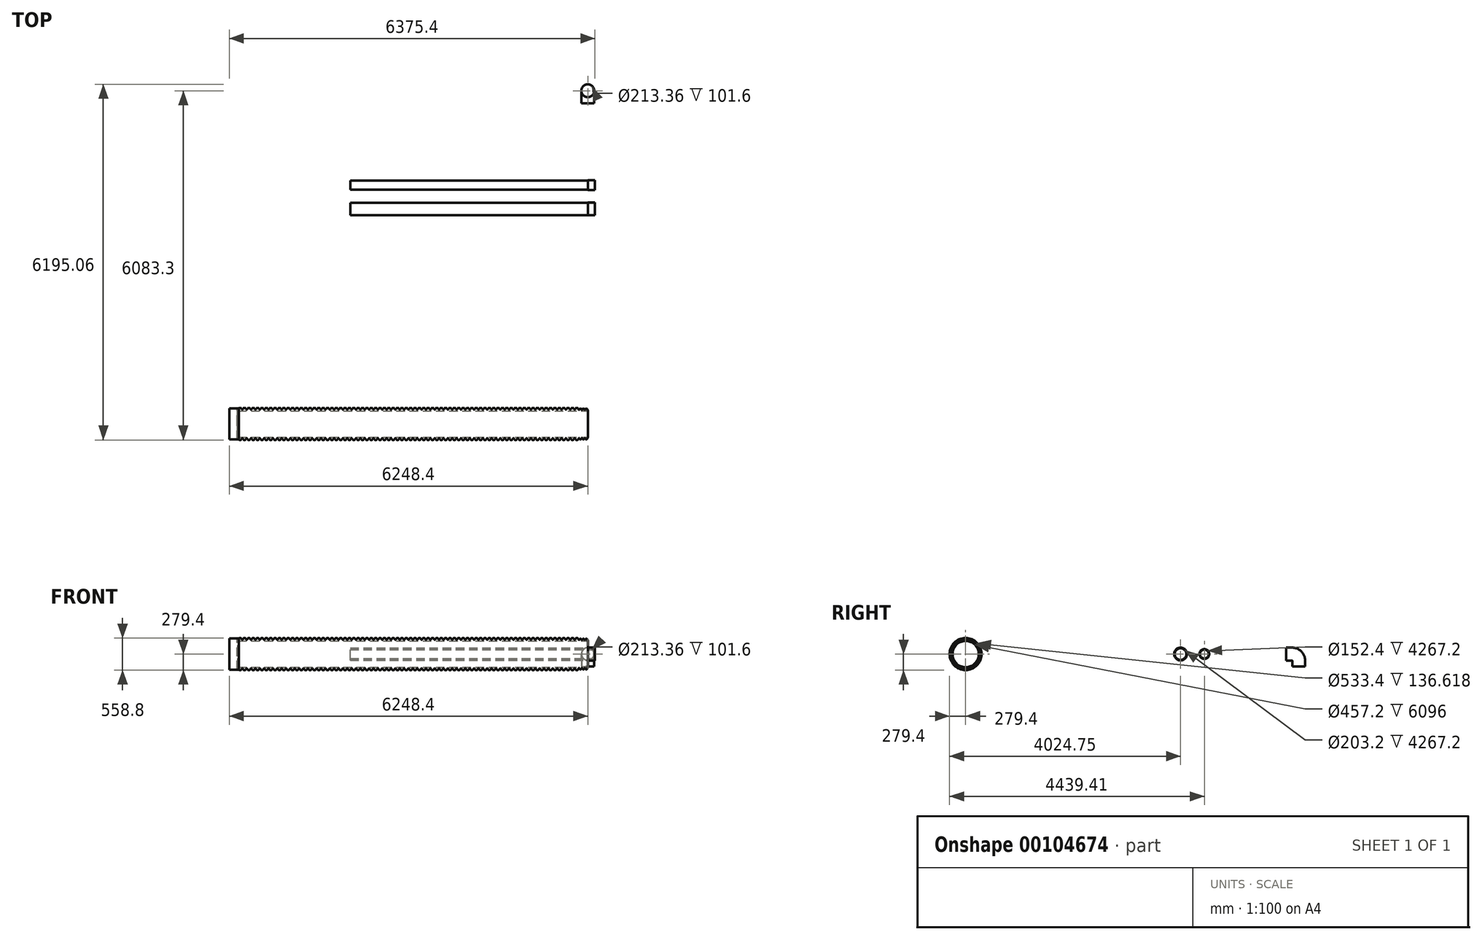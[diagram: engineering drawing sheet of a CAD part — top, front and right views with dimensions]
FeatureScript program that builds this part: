
annotation { "Feature Type Name" : "Feature", "Feature Type Description" : "" }
export const myFeature = defineFeature(function(context is Context, id is Id, definition is map)
    precondition{}
    {
        {
            var Q0;
            Q0=qCreatedBy(makeId("Right.planeOp"),FACE);
            var sketch = newSketch(context, id + "F0", { "sketchPlane" : qUnion([Q0])});
            skLineSegment(sketch, "E0", {"start": v(0, 0) * mm, "end": v(3048, 0) * mm, "construction": true});
            skCircle(sketch, "E1", {"center": v(0, 0) * mm, "radius": 228.6 * mm});
            skCircle(sketch, "E2", {"center": v(0, 0) * mm, "radius": 279.4 * mm});
            skCircle(sketch, "E3", {"center": v(697.35, 0) * mm, "radius": 106.68 * mm});
            skCircle(sketch, "E4", {"center": v(697.35, 0) * mm, "radius": 101.6 * mm});
            skCircle(sketch, "E5", {"center": v(1112.01, 0) * mm, "radius": 76.2 * mm});
            skCircle(sketch, "E6", {"center": v(1112.01, 0) * mm, "radius": 81.28 * mm});
            skCircle(sketch, "E7", {"center": v(697.35, 0) * mm, "radius": 111.76 * mm});
            skCircle(sketch, "E8", {"center": v(1112.01, 0) * mm, "radius": 86.36 * mm});
            skCircle(sketch, "E9", {"center": v(0, 0) * mm, "radius": 304.8 * mm});
            skSolve(sketch);
        }
        {
            var Q0;
            Q0=makeQuery(id+"F0.imprint","IMPRINT",FACE,{"disambiguationData":[TD([[makeQuery(id+"F0.imprint","IMPRINT",EDGE,{"derivedFrom":sQuery(id+"F0.wireOp",EDGE,"E5")}),-1.0]])]});
            var Q1;
            Q1=makeQuery(id+"F0.imprint","IMPRINT",FACE,{"disambiguationData":[TD([[makeQuery(id+"F0.imprint","IMPRINT",EDGE,{"derivedFrom":sQuery(id+"F0.wireOp",EDGE,"E3")}),1.0]])]});
            extrude(context, id + "F1", {"entities" : qUnion([Q0, Q1]), "oppositeDirection" : true, "depth" : 4140.2 * mm});
        }
        {
            var Q0;
            Q0=makeQuery(id+"F0.imprint","IMPRINT",FACE,{"disambiguationData":[TD([[makeQuery(id+"F0.imprint","IMPRINT",EDGE,{"derivedFrom":sQuery(id+"F0.wireOp",EDGE,"E3")}),1.0]])]});
            var Q1;
            Q1=makeQuery(id+"F0.imprint","IMPRINT",FACE,{"disambiguationData":[TD([[makeQuery(id+"F0.imprint","IMPRINT",EDGE,{"derivedFrom":sQuery(id+"F0.wireOp",EDGE,"E3")}),-1.0]])]});
            extrude(context, id + "F2", {"entities" : qUnion([Q0, Q1]), "operationType" : NewBodyOperationType.ADD, "depth" : 127 * mm});
        }
        {
            var Q0;
            Q0=makeQuery(id+"F0.imprint","IMPRINT",FACE,{"disambiguationData":[TD([[makeQuery(id+"F0.imprint","IMPRINT",EDGE,{"derivedFrom":sQuery(id+"F0.wireOp",EDGE,"E6")}),-1.0]])]});
            var Q1;
            Q1=makeQuery(id+"F0.imprint","IMPRINT",FACE,{"disambiguationData":[TD([[makeQuery(id+"F0.imprint","IMPRINT",EDGE,{"derivedFrom":sQuery(id+"F0.wireOp",EDGE,"E5")}),-1.0]])]});
            extrude(context, id + "F3", {"entities" : qUnion([Q0, Q1]), "operationType" : NewBodyOperationType.ADD, "depth" : 127 * mm});
        }
        {
            var Q0;
            Q0=makeQuery(id+"F3.opExtrude","CAP_EDGE",EDGE,{"disambiguationData":[OSD([sQuery(id+"F0.wireOp",EDGE,"E8")])],"isStart":true});
            var Q1;
            Q1=makeQuery(id+"F2.opExtrude","CAP_EDGE",EDGE,{"disambiguationData":[OSD([sQuery(id+"F0.wireOp",EDGE,"E7")])],"isStart":true});
            chamfer(context, id + "F4", {"entities" : qUnion([Q0, Q1]), "width" : 5.08 * mm, "tangentPropagation" : true});
        }
        {
            var Q0;
            Q0=qCreatedBy(makeId("Front.planeOp"),FACE);
            cPlane(context, id + "F5", {"entities" : qUnion([Q0]), "cplaneType" : CPlaneType.OFFSET, "offset" : 3048 * mm, "width" : 152.4 * mm, "height" : 152.4 * mm});
        }
        {
            var Q0;
            Q0=qCreatedBy(id+"F5.planeOp",FACE);
            var sketch = newSketch(context, id + "F6", { "sketchPlane" : qUnion([Q0])});
            skLineSegment(sketch, "E10", {"start": v(0, 0) * mm, "end": v(-6096, 0) * mm, "construction": true});
            skLineSegment(sketch, "E11", {"start": v(0, 228.6) * mm, "end": v(-6096, 228.6) * mm});
            skLineSegment(sketch, "E12", {"start": v(0, 233.68) * mm, "end": v(-304.8, 233.68) * mm, "construction": true});
            skLineSegment(sketch, "E13", {"start": v(0, 233.68) * mm, "end": v(-10.43, 258.86) * mm});
            skLineSegment(sketch, "E14", {"start": v(-22.16, 266.7) * mm, "end": v(-28.64, 266.7) * mm});
            skLineSegment(sketch, "E15", {"start": v(-40.37, 258.86) * mm, "end": v(-44.93, 247.84) * mm});
            skPoint(sketch, "E16.visualSharp", {"position": v(-37.12, 266.7) * mm});
            skArc(sketch, "E16.filletArc", {"start": v(-28.64, 266.7) * mm, "mid": v(-35.7, 264.56) * mm, "end": v(-40.37, 258.86) * mm});
            skPoint(sketch, "E17.visualSharp", {"position": v(-13.68, 266.7) * mm});
            skArc(sketch, "E17.filletArc", {"start": v(-10.43, 258.86) * mm, "mid": v(-15.1, 264.56) * mm, "end": v(-22.16, 266.7) * mm});
            skArc(sketch, "E18.1.0.0", {"start": v(-79.44, 266.7) * mm, "mid": v(-86.5, 264.56) * mm, "end": v(-91.17, 258.86) * mm});
            skLineSegment(sketch, "E18.1.0.1", {"start": v(-91.17, 258.86) * mm, "end": v(-95.73, 247.84) * mm});
            skPoint(sketch, "E18.1.0.2", {"position": v(-87.92, 266.7) * mm});
            skArc(sketch, "E18.1.0.3", {"start": v(-61.23, 258.86) * mm, "mid": v(-65.9, 264.56) * mm, "end": v(-72.96, 266.7) * mm});
            skPoint(sketch, "E18.1.0.4", {"position": v(-64.48, 266.7) * mm});
            skLineSegment(sketch, "E18.1.0.5", {"start": v(-56.67, 247.84) * mm, "end": v(-61.23, 258.86) * mm});
            skLineSegment(sketch, "E18.1.0.6", {"start": v(-72.96, 266.7) * mm, "end": v(-79.44, 266.7) * mm});
            skArc(sketch, "E18.2.0.0", {"start": v(-130.24, 266.7) * mm, "mid": v(-137.3, 264.56) * mm, "end": v(-141.97, 258.86) * mm});
            skLineSegment(sketch, "E18.2.0.1", {"start": v(-141.97, 258.86) * mm, "end": v(-146.53, 247.84) * mm});
            skPoint(sketch, "E18.2.0.2", {"position": v(-138.72, 266.7) * mm});
            skArc(sketch, "E18.2.0.3", {"start": v(-112.03, 258.86) * mm, "mid": v(-116.7, 264.56) * mm, "end": v(-123.76, 266.7) * mm});
            skPoint(sketch, "E18.2.0.4", {"position": v(-115.28, 266.7) * mm});
            skLineSegment(sketch, "E18.2.0.5", {"start": v(-107.47, 247.84) * mm, "end": v(-112.03, 258.86) * mm});
            skLineSegment(sketch, "E18.2.0.6", {"start": v(-123.76, 266.7) * mm, "end": v(-130.24, 266.7) * mm});
            skLineSegment(sketch, "E18.direction1", {"start": v(-50.8, 233.68) * mm, "end": v(-101.6, 233.68) * mm, "construction": true});
            skPoint(sketch, "E19.visualSharp", {"position": v(-101.6, 233.68) * mm});
            skArc(sketch, "E19.filletArc", {"start": v(-107.47, 247.84) * mm, "mid": v(-101.6, 243.92) * mm, "end": v(-95.73, 247.84) * mm});
            skPoint(sketch, "E20.visualSharp", {"position": v(-50.8, 233.68) * mm});
            skArc(sketch, "E20.filletArc", {"start": v(-56.67, 247.84) * mm, "mid": v(-50.8, 243.92) * mm, "end": v(-44.93, 247.84) * mm});
            skLineSegment(sketch, "E21", {"start": v(-158.27, 247.84) * mm, "end": v(-166.47, 267.64) * mm});
            skLineSegment(sketch, "E22", {"start": v(-184.07, 279.4) * mm, "end": v(-196.93, 279.4) * mm});
            skLineSegment(sketch, "E23", {"start": v(-214.53, 267.64) * mm, "end": v(-219.8, 254.92) * mm});
            skPoint(sketch, "E24.visualSharp", {"position": v(-209.66, 279.4) * mm});
            skArc(sketch, "E24.filletArc", {"start": v(-196.93, 279.4) * mm, "mid": v(-207.52, 276.19) * mm, "end": v(-214.53, 267.64) * mm});
            skPoint(sketch, "E25.visualSharp", {"position": v(-171.34, 279.4) * mm});
            skArc(sketch, "E25.filletArc", {"start": v(-166.47, 267.64) * mm, "mid": v(-173.48, 276.19) * mm, "end": v(-184.07, 279.4) * mm});
            skPoint(sketch, "E26.visualSharp", {"position": v(-152.4, 233.68) * mm});
            skArc(sketch, "E26.filletArc", {"start": v(-158.27, 247.84) * mm, "mid": v(-152.4, 243.92) * mm, "end": v(-146.53, 247.84) * mm});
            skLineSegment(sketch, "E27", {"start": v(-237.4, 254.92) * mm, "end": v(-242.67, 267.64) * mm});
            skPoint(sketch, "E28.visualSharp", {"position": v(-228.6, 233.68) * mm});
            skArc(sketch, "E28.filletArc", {"start": v(-237.4, 254.92) * mm, "mid": v(-228.6, 249.05) * mm, "end": v(-219.8, 254.92) * mm});
            skLineSegment(sketch, "E29", {"start": v(-260.27, 279.4) * mm, "end": v(-273.13, 279.4) * mm});
            skLineSegment(sketch, "E30", {"start": v(-290.73, 267.64) * mm, "end": v(-296, 254.92) * mm});
            skPoint(sketch, "E31.visualSharp", {"position": v(-285.86, 279.4) * mm});
            skArc(sketch, "E31.filletArc", {"start": v(-273.13, 279.4) * mm, "mid": v(-283.72, 276.19) * mm, "end": v(-290.73, 267.64) * mm});
            skPoint(sketch, "E32.visualSharp", {"position": v(-247.54, 279.4) * mm});
            skArc(sketch, "E32.filletArc", {"start": v(-242.67, 267.64) * mm, "mid": v(-249.68, 276.19) * mm, "end": v(-260.27, 279.4) * mm});
            skLineSegment(sketch, "E33", {"start": v(-237.4, 254.92) * mm, "end": v(-296, 254.92) * mm, "construction": true});
            skPoint(sketch, "E34.orphan", {"position": v(-304.8, 233.68) * mm});
            skArc(sketch, "E35.1.0.0", {"start": v(-313.6, 254.92) * mm, "mid": v(-304.8, 249.05) * mm, "end": v(-296, 254.92) * mm});
            skLineSegment(sketch, "E35.1.0.1", {"start": v(-313.6, 254.92) * mm, "end": v(-318.87, 267.64) * mm});
            skArc(sketch, "E35.1.0.2", {"start": v(-318.87, 267.64) * mm, "mid": v(-325.88, 276.19) * mm, "end": v(-336.47, 279.4) * mm});
            skLineSegment(sketch, "E35.1.0.3", {"start": v(-336.47, 279.4) * mm, "end": v(-349.33, 279.4) * mm});
            skArc(sketch, "E35.1.0.4", {"start": v(-349.33, 279.4) * mm, "mid": v(-359.92, 276.19) * mm, "end": v(-366.93, 267.64) * mm});
            skLineSegment(sketch, "E35.1.0.5", {"start": v(-366.93, 267.64) * mm, "end": v(-372.2, 254.92) * mm});
            skArc(sketch, "E35.2.0.0", {"start": v(-389.8, 254.92) * mm, "mid": v(-381, 249.05) * mm, "end": v(-372.2, 254.92) * mm});
            skLineSegment(sketch, "E35.2.0.1", {"start": v(-389.8, 254.92) * mm, "end": v(-395.07, 267.64) * mm});
            skArc(sketch, "E35.2.0.2", {"start": v(-395.07, 267.64) * mm, "mid": v(-402.08, 276.19) * mm, "end": v(-412.67, 279.4) * mm});
            skLineSegment(sketch, "E35.2.0.3", {"start": v(-412.67, 279.4) * mm, "end": v(-425.53, 279.4) * mm});
            skArc(sketch, "E35.2.0.4", {"start": v(-425.53, 279.4) * mm, "mid": v(-436.12, 276.19) * mm, "end": v(-443.13, 267.64) * mm});
            skLineSegment(sketch, "E35.2.0.5", {"start": v(-443.13, 267.64) * mm, "end": v(-448.4, 254.92) * mm});
            skArc(sketch, "E35.3.0.0", {"start": v(-466, 254.92) * mm, "mid": v(-457.2, 249.05) * mm, "end": v(-448.4, 254.92) * mm});
            skLineSegment(sketch, "E35.3.0.1", {"start": v(-466, 254.92) * mm, "end": v(-471.27, 267.64) * mm});
            skArc(sketch, "E35.3.0.2", {"start": v(-471.27, 267.64) * mm, "mid": v(-478.28, 276.19) * mm, "end": v(-488.87, 279.4) * mm});
            skLineSegment(sketch, "E35.3.0.3", {"start": v(-488.87, 279.4) * mm, "end": v(-501.73, 279.4) * mm});
            skArc(sketch, "E35.3.0.4", {"start": v(-501.73, 279.4) * mm, "mid": v(-512.32, 276.19) * mm, "end": v(-519.33, 267.64) * mm});
            skLineSegment(sketch, "E35.3.0.5", {"start": v(-519.33, 267.64) * mm, "end": v(-524.6, 254.92) * mm});
            skArc(sketch, "E35.4.0.0", {"start": v(-542.2, 254.92) * mm, "mid": v(-533.4, 249.05) * mm, "end": v(-524.6, 254.92) * mm});
            skLineSegment(sketch, "E35.4.0.1", {"start": v(-542.2, 254.92) * mm, "end": v(-547.47, 267.64) * mm});
            skArc(sketch, "E35.4.0.2", {"start": v(-547.47, 267.64) * mm, "mid": v(-554.48, 276.19) * mm, "end": v(-565.07, 279.4) * mm});
            skLineSegment(sketch, "E35.4.0.3", {"start": v(-565.07, 279.4) * mm, "end": v(-577.93, 279.4) * mm});
            skArc(sketch, "E35.4.0.4", {"start": v(-577.93, 279.4) * mm, "mid": v(-588.52, 276.19) * mm, "end": v(-595.53, 267.64) * mm});
            skLineSegment(sketch, "E35.4.0.5", {"start": v(-595.53, 267.64) * mm, "end": v(-600.8, 254.92) * mm});
            skArc(sketch, "E35.5.0.0", {"start": v(-618.4, 254.92) * mm, "mid": v(-609.6, 249.05) * mm, "end": v(-600.8, 254.92) * mm});
            skLineSegment(sketch, "E35.5.0.1", {"start": v(-618.4, 254.92) * mm, "end": v(-623.67, 267.64) * mm});
            skArc(sketch, "E35.5.0.2", {"start": v(-623.67, 267.64) * mm, "mid": v(-630.68, 276.19) * mm, "end": v(-641.27, 279.4) * mm});
            skLineSegment(sketch, "E35.5.0.3", {"start": v(-641.27, 279.4) * mm, "end": v(-654.13, 279.4) * mm});
            skArc(sketch, "E35.5.0.4", {"start": v(-654.13, 279.4) * mm, "mid": v(-664.72, 276.19) * mm, "end": v(-671.73, 267.64) * mm});
            skLineSegment(sketch, "E35.5.0.5", {"start": v(-671.73, 267.64) * mm, "end": v(-677, 254.92) * mm});
            skArc(sketch, "E35.6.0.0", {"start": v(-694.6, 254.92) * mm, "mid": v(-685.8, 249.05) * mm, "end": v(-677, 254.92) * mm});
            skLineSegment(sketch, "E35.6.0.1", {"start": v(-694.6, 254.92) * mm, "end": v(-699.87, 267.64) * mm});
            skArc(sketch, "E35.6.0.2", {"start": v(-699.87, 267.64) * mm, "mid": v(-706.88, 276.19) * mm, "end": v(-717.47, 279.4) * mm});
            skLineSegment(sketch, "E35.6.0.3", {"start": v(-717.47, 279.4) * mm, "end": v(-730.33, 279.4) * mm});
            skArc(sketch, "E35.6.0.4", {"start": v(-730.33, 279.4) * mm, "mid": v(-740.92, 276.19) * mm, "end": v(-747.93, 267.64) * mm});
            skLineSegment(sketch, "E35.6.0.5", {"start": v(-747.93, 267.64) * mm, "end": v(-753.2, 254.92) * mm});
            skArc(sketch, "E35.7.0.0", {"start": v(-770.8, 254.92) * mm, "mid": v(-762, 249.05) * mm, "end": v(-753.2, 254.92) * mm});
            skLineSegment(sketch, "E35.7.0.1", {"start": v(-770.8, 254.92) * mm, "end": v(-776.07, 267.64) * mm});
            skArc(sketch, "E35.7.0.2", {"start": v(-776.07, 267.64) * mm, "mid": v(-783.08, 276.19) * mm, "end": v(-793.67, 279.4) * mm});
            skLineSegment(sketch, "E35.7.0.3", {"start": v(-793.67, 279.4) * mm, "end": v(-806.53, 279.4) * mm});
            skArc(sketch, "E35.7.0.4", {"start": v(-806.53, 279.4) * mm, "mid": v(-817.12, 276.19) * mm, "end": v(-824.13, 267.64) * mm});
            skLineSegment(sketch, "E35.7.0.5", {"start": v(-824.13, 267.64) * mm, "end": v(-829.4, 254.92) * mm});
            skArc(sketch, "E35.8.0.0", {"start": v(-847, 254.92) * mm, "mid": v(-838.2, 249.05) * mm, "end": v(-829.4, 254.92) * mm});
            skLineSegment(sketch, "E35.8.0.1", {"start": v(-847, 254.92) * mm, "end": v(-852.27, 267.64) * mm});
            skArc(sketch, "E35.8.0.2", {"start": v(-852.27, 267.64) * mm, "mid": v(-859.28, 276.19) * mm, "end": v(-869.87, 279.4) * mm});
            skLineSegment(sketch, "E35.8.0.3", {"start": v(-869.87, 279.4) * mm, "end": v(-882.73, 279.4) * mm});
            skArc(sketch, "E35.8.0.4", {"start": v(-882.73, 279.4) * mm, "mid": v(-893.32, 276.19) * mm, "end": v(-900.33, 267.64) * mm});
            skLineSegment(sketch, "E35.8.0.5", {"start": v(-900.33, 267.64) * mm, "end": v(-905.6, 254.92) * mm});
            skArc(sketch, "E35.9.0.0", {"start": v(-923.2, 254.92) * mm, "mid": v(-914.4, 249.05) * mm, "end": v(-905.6, 254.92) * mm});
            skLineSegment(sketch, "E35.9.0.1", {"start": v(-923.2, 254.92) * mm, "end": v(-928.47, 267.64) * mm});
            skArc(sketch, "E35.9.0.2", {"start": v(-928.47, 267.64) * mm, "mid": v(-935.48, 276.19) * mm, "end": v(-946.07, 279.4) * mm});
            skLineSegment(sketch, "E35.9.0.3", {"start": v(-946.07, 279.4) * mm, "end": v(-958.93, 279.4) * mm});
            skArc(sketch, "E35.9.0.4", {"start": v(-958.93, 279.4) * mm, "mid": v(-969.52, 276.19) * mm, "end": v(-976.53, 267.64) * mm});
            skLineSegment(sketch, "E35.9.0.5", {"start": v(-976.53, 267.64) * mm, "end": v(-981.8, 254.92) * mm});
            skArc(sketch, "E35.10.0.0", {"start": v(-999.4, 254.92) * mm, "mid": v(-990.6, 249.05) * mm, "end": v(-981.8, 254.92) * mm});
            skLineSegment(sketch, "E35.10.0.1", {"start": v(-999.4, 254.92) * mm, "end": v(-1004.67, 267.64) * mm});
            skArc(sketch, "E35.10.0.2", {"start": v(-1004.67, 267.64) * mm, "mid": v(-1011.68, 276.19) * mm, "end": v(-1022.27, 279.4) * mm});
            skLineSegment(sketch, "E35.10.0.3", {"start": v(-1022.27, 279.4) * mm, "end": v(-1035.13, 279.4) * mm});
            skArc(sketch, "E35.10.0.4", {"start": v(-1035.13, 279.4) * mm, "mid": v(-1045.72, 276.19) * mm, "end": v(-1052.73, 267.64) * mm});
            skLineSegment(sketch, "E35.10.0.5", {"start": v(-1052.73, 267.64) * mm, "end": v(-1058, 254.92) * mm});
            skArc(sketch, "E35.11.0.0", {"start": v(-1075.6, 254.92) * mm, "mid": v(-1066.8, 249.05) * mm, "end": v(-1058, 254.92) * mm});
            skLineSegment(sketch, "E35.11.0.1", {"start": v(-1075.6, 254.92) * mm, "end": v(-1080.87, 267.64) * mm});
            skArc(sketch, "E35.11.0.2", {"start": v(-1080.87, 267.64) * mm, "mid": v(-1087.88, 276.19) * mm, "end": v(-1098.47, 279.4) * mm});
            skLineSegment(sketch, "E35.11.0.3", {"start": v(-1098.47, 279.4) * mm, "end": v(-1111.33, 279.4) * mm});
            skArc(sketch, "E35.11.0.4", {"start": v(-1111.33, 279.4) * mm, "mid": v(-1121.92, 276.19) * mm, "end": v(-1128.93, 267.64) * mm});
            skLineSegment(sketch, "E35.11.0.5", {"start": v(-1128.93, 267.64) * mm, "end": v(-1134.2, 254.92) * mm});
            skArc(sketch, "E35.12.0.0", {"start": v(-1151.8, 254.92) * mm, "mid": v(-1143, 249.05) * mm, "end": v(-1134.2, 254.92) * mm});
            skLineSegment(sketch, "E35.12.0.1", {"start": v(-1151.8, 254.92) * mm, "end": v(-1157.07, 267.64) * mm});
            skArc(sketch, "E35.12.0.2", {"start": v(-1157.07, 267.64) * mm, "mid": v(-1164.08, 276.19) * mm, "end": v(-1174.67, 279.4) * mm});
            skLineSegment(sketch, "E35.12.0.3", {"start": v(-1174.67, 279.4) * mm, "end": v(-1187.53, 279.4) * mm});
            skArc(sketch, "E35.12.0.4", {"start": v(-1187.53, 279.4) * mm, "mid": v(-1198.12, 276.19) * mm, "end": v(-1205.13, 267.64) * mm});
            skLineSegment(sketch, "E35.12.0.5", {"start": v(-1205.13, 267.64) * mm, "end": v(-1210.4, 254.92) * mm});
            skArc(sketch, "E35.13.0.0", {"start": v(-1228, 254.92) * mm, "mid": v(-1219.2, 249.05) * mm, "end": v(-1210.4, 254.92) * mm});
            skLineSegment(sketch, "E35.13.0.1", {"start": v(-1228, 254.92) * mm, "end": v(-1233.27, 267.64) * mm});
            skArc(sketch, "E35.13.0.2", {"start": v(-1233.27, 267.64) * mm, "mid": v(-1240.28, 276.19) * mm, "end": v(-1250.87, 279.4) * mm});
            skLineSegment(sketch, "E35.13.0.3", {"start": v(-1250.87, 279.4) * mm, "end": v(-1263.73, 279.4) * mm});
            skArc(sketch, "E35.13.0.4", {"start": v(-1263.73, 279.4) * mm, "mid": v(-1274.32, 276.19) * mm, "end": v(-1281.33, 267.64) * mm});
            skLineSegment(sketch, "E35.13.0.5", {"start": v(-1281.33, 267.64) * mm, "end": v(-1286.6, 254.92) * mm});
            skArc(sketch, "E35.14.0.0", {"start": v(-1304.2, 254.92) * mm, "mid": v(-1295.4, 249.05) * mm, "end": v(-1286.6, 254.92) * mm});
            skLineSegment(sketch, "E35.14.0.1", {"start": v(-1304.2, 254.92) * mm, "end": v(-1309.47, 267.64) * mm});
            skArc(sketch, "E35.14.0.2", {"start": v(-1309.47, 267.64) * mm, "mid": v(-1316.48, 276.19) * mm, "end": v(-1327.07, 279.4) * mm});
            skLineSegment(sketch, "E35.14.0.3", {"start": v(-1327.07, 279.4) * mm, "end": v(-1339.93, 279.4) * mm});
            skArc(sketch, "E35.14.0.4", {"start": v(-1339.93, 279.4) * mm, "mid": v(-1350.52, 276.19) * mm, "end": v(-1357.53, 267.64) * mm});
            skLineSegment(sketch, "E35.14.0.5", {"start": v(-1357.53, 267.64) * mm, "end": v(-1362.8, 254.92) * mm});
            skArc(sketch, "E35.15.0.0", {"start": v(-1380.4, 254.92) * mm, "mid": v(-1371.6, 249.05) * mm, "end": v(-1362.8, 254.92) * mm});
            skLineSegment(sketch, "E35.15.0.1", {"start": v(-1380.4, 254.92) * mm, "end": v(-1385.67, 267.64) * mm});
            skArc(sketch, "E35.15.0.2", {"start": v(-1385.67, 267.64) * mm, "mid": v(-1392.68, 276.19) * mm, "end": v(-1403.27, 279.4) * mm});
            skLineSegment(sketch, "E35.15.0.3", {"start": v(-1403.27, 279.4) * mm, "end": v(-1416.13, 279.4) * mm});
            skArc(sketch, "E35.15.0.4", {"start": v(-1416.13, 279.4) * mm, "mid": v(-1426.72, 276.19) * mm, "end": v(-1433.73, 267.64) * mm});
            skLineSegment(sketch, "E35.15.0.5", {"start": v(-1433.73, 267.64) * mm, "end": v(-1439, 254.92) * mm});
            skArc(sketch, "E35.16.0.0", {"start": v(-1456.6, 254.92) * mm, "mid": v(-1447.8, 249.05) * mm, "end": v(-1439, 254.92) * mm});
            skLineSegment(sketch, "E35.16.0.1", {"start": v(-1456.6, 254.92) * mm, "end": v(-1461.87, 267.64) * mm});
            skArc(sketch, "E35.16.0.2", {"start": v(-1461.87, 267.64) * mm, "mid": v(-1468.88, 276.19) * mm, "end": v(-1479.47, 279.4) * mm});
            skLineSegment(sketch, "E35.16.0.3", {"start": v(-1479.47, 279.4) * mm, "end": v(-1492.33, 279.4) * mm});
            skArc(sketch, "E35.16.0.4", {"start": v(-1492.33, 279.4) * mm, "mid": v(-1502.92, 276.19) * mm, "end": v(-1509.93, 267.64) * mm});
            skLineSegment(sketch, "E35.16.0.5", {"start": v(-1509.93, 267.64) * mm, "end": v(-1515.2, 254.92) * mm});
            skArc(sketch, "E35.17.0.0", {"start": v(-1532.8, 254.92) * mm, "mid": v(-1524, 249.05) * mm, "end": v(-1515.2, 254.92) * mm});
            skLineSegment(sketch, "E35.17.0.1", {"start": v(-1532.8, 254.92) * mm, "end": v(-1538.07, 267.64) * mm});
            skArc(sketch, "E35.17.0.2", {"start": v(-1538.07, 267.64) * mm, "mid": v(-1545.08, 276.19) * mm, "end": v(-1555.67, 279.4) * mm});
            skLineSegment(sketch, "E35.17.0.3", {"start": v(-1555.67, 279.4) * mm, "end": v(-1568.53, 279.4) * mm});
            skArc(sketch, "E35.17.0.4", {"start": v(-1568.53, 279.4) * mm, "mid": v(-1579.12, 276.19) * mm, "end": v(-1586.13, 267.64) * mm});
            skLineSegment(sketch, "E35.17.0.5", {"start": v(-1586.13, 267.64) * mm, "end": v(-1591.4, 254.92) * mm});
            skArc(sketch, "E35.18.0.0", {"start": v(-1609, 254.92) * mm, "mid": v(-1600.2, 249.05) * mm, "end": v(-1591.4, 254.92) * mm});
            skLineSegment(sketch, "E35.18.0.1", {"start": v(-1609, 254.92) * mm, "end": v(-1614.27, 267.64) * mm});
            skArc(sketch, "E35.18.0.2", {"start": v(-1614.27, 267.64) * mm, "mid": v(-1621.28, 276.19) * mm, "end": v(-1631.87, 279.4) * mm});
            skLineSegment(sketch, "E35.18.0.3", {"start": v(-1631.87, 279.4) * mm, "end": v(-1644.73, 279.4) * mm});
            skArc(sketch, "E35.18.0.4", {"start": v(-1644.73, 279.4) * mm, "mid": v(-1655.32, 276.19) * mm, "end": v(-1662.33, 267.64) * mm});
            skLineSegment(sketch, "E35.18.0.5", {"start": v(-1662.33, 267.64) * mm, "end": v(-1667.6, 254.92) * mm});
            skArc(sketch, "E35.19.0.0", {"start": v(-1685.2, 254.92) * mm, "mid": v(-1676.4, 249.05) * mm, "end": v(-1667.6, 254.92) * mm});
            skLineSegment(sketch, "E35.19.0.1", {"start": v(-1685.2, 254.92) * mm, "end": v(-1690.47, 267.64) * mm});
            skArc(sketch, "E35.19.0.2", {"start": v(-1690.47, 267.64) * mm, "mid": v(-1697.48, 276.19) * mm, "end": v(-1708.07, 279.4) * mm});
            skLineSegment(sketch, "E35.19.0.3", {"start": v(-1708.07, 279.4) * mm, "end": v(-1720.93, 279.4) * mm});
            skArc(sketch, "E35.19.0.4", {"start": v(-1720.93, 279.4) * mm, "mid": v(-1731.52, 276.19) * mm, "end": v(-1738.53, 267.64) * mm});
            skLineSegment(sketch, "E35.19.0.5", {"start": v(-1738.53, 267.64) * mm, "end": v(-1743.8, 254.92) * mm});
            skArc(sketch, "E35.20.0.0", {"start": v(-1761.4, 254.92) * mm, "mid": v(-1752.6, 249.05) * mm, "end": v(-1743.8, 254.92) * mm});
            skLineSegment(sketch, "E35.20.0.1", {"start": v(-1761.4, 254.92) * mm, "end": v(-1766.67, 267.64) * mm});
            skArc(sketch, "E35.20.0.2", {"start": v(-1766.67, 267.64) * mm, "mid": v(-1773.68, 276.19) * mm, "end": v(-1784.27, 279.4) * mm});
            skLineSegment(sketch, "E35.20.0.3", {"start": v(-1784.27, 279.4) * mm, "end": v(-1797.13, 279.4) * mm});
            skArc(sketch, "E35.20.0.4", {"start": v(-1797.13, 279.4) * mm, "mid": v(-1807.72, 276.19) * mm, "end": v(-1814.73, 267.64) * mm});
            skLineSegment(sketch, "E35.20.0.5", {"start": v(-1814.73, 267.64) * mm, "end": v(-1820, 254.92) * mm});
            skArc(sketch, "E35.21.0.0", {"start": v(-1837.6, 254.92) * mm, "mid": v(-1828.8, 249.05) * mm, "end": v(-1820, 254.92) * mm});
            skLineSegment(sketch, "E35.21.0.1", {"start": v(-1837.6, 254.92) * mm, "end": v(-1842.87, 267.64) * mm});
            skArc(sketch, "E35.21.0.2", {"start": v(-1842.87, 267.64) * mm, "mid": v(-1849.88, 276.19) * mm, "end": v(-1860.47, 279.4) * mm});
            skLineSegment(sketch, "E35.21.0.3", {"start": v(-1860.47, 279.4) * mm, "end": v(-1873.33, 279.4) * mm});
            skArc(sketch, "E35.21.0.4", {"start": v(-1873.33, 279.4) * mm, "mid": v(-1883.92, 276.19) * mm, "end": v(-1890.93, 267.64) * mm});
            skLineSegment(sketch, "E35.21.0.5", {"start": v(-1890.93, 267.64) * mm, "end": v(-1896.2, 254.92) * mm});
            skArc(sketch, "E35.22.0.0", {"start": v(-1913.8, 254.92) * mm, "mid": v(-1905, 249.05) * mm, "end": v(-1896.2, 254.92) * mm});
            skLineSegment(sketch, "E35.22.0.1", {"start": v(-1913.8, 254.92) * mm, "end": v(-1919.07, 267.64) * mm});
            skArc(sketch, "E35.22.0.2", {"start": v(-1919.07, 267.64) * mm, "mid": v(-1926.08, 276.19) * mm, "end": v(-1936.67, 279.4) * mm});
            skLineSegment(sketch, "E35.22.0.3", {"start": v(-1936.67, 279.4) * mm, "end": v(-1949.53, 279.4) * mm});
            skArc(sketch, "E35.22.0.4", {"start": v(-1949.53, 279.4) * mm, "mid": v(-1960.12, 276.19) * mm, "end": v(-1967.13, 267.64) * mm});
            skLineSegment(sketch, "E35.22.0.5", {"start": v(-1967.13, 267.64) * mm, "end": v(-1972.4, 254.92) * mm});
            skArc(sketch, "E35.23.0.0", {"start": v(-1990, 254.92) * mm, "mid": v(-1981.2, 249.05) * mm, "end": v(-1972.4, 254.92) * mm});
            skLineSegment(sketch, "E35.23.0.1", {"start": v(-1990, 254.92) * mm, "end": v(-1995.27, 267.64) * mm});
            skArc(sketch, "E35.23.0.2", {"start": v(-1995.27, 267.64) * mm, "mid": v(-2002.28, 276.19) * mm, "end": v(-2012.87, 279.4) * mm});
            skLineSegment(sketch, "E35.23.0.3", {"start": v(-2012.87, 279.4) * mm, "end": v(-2025.73, 279.4) * mm});
            skArc(sketch, "E35.23.0.4", {"start": v(-2025.73, 279.4) * mm, "mid": v(-2036.32, 276.19) * mm, "end": v(-2043.33, 267.64) * mm});
            skLineSegment(sketch, "E35.23.0.5", {"start": v(-2043.33, 267.64) * mm, "end": v(-2048.6, 254.92) * mm});
            skArc(sketch, "E35.24.0.0", {"start": v(-2066.2, 254.92) * mm, "mid": v(-2057.4, 249.05) * mm, "end": v(-2048.6, 254.92) * mm});
            skLineSegment(sketch, "E35.24.0.1", {"start": v(-2066.2, 254.92) * mm, "end": v(-2071.47, 267.64) * mm});
            skArc(sketch, "E35.24.0.2", {"start": v(-2071.47, 267.64) * mm, "mid": v(-2078.48, 276.19) * mm, "end": v(-2089.07, 279.4) * mm});
            skLineSegment(sketch, "E35.24.0.3", {"start": v(-2089.07, 279.4) * mm, "end": v(-2101.93, 279.4) * mm});
            skArc(sketch, "E35.24.0.4", {"start": v(-2101.93, 279.4) * mm, "mid": v(-2112.52, 276.19) * mm, "end": v(-2119.53, 267.64) * mm});
            skLineSegment(sketch, "E35.24.0.5", {"start": v(-2119.53, 267.64) * mm, "end": v(-2124.8, 254.92) * mm});
            skArc(sketch, "E35.25.0.0", {"start": v(-2142.4, 254.92) * mm, "mid": v(-2133.6, 249.05) * mm, "end": v(-2124.8, 254.92) * mm});
            skLineSegment(sketch, "E35.25.0.1", {"start": v(-2142.4, 254.92) * mm, "end": v(-2147.67, 267.64) * mm});
            skArc(sketch, "E35.25.0.2", {"start": v(-2147.67, 267.64) * mm, "mid": v(-2154.68, 276.19) * mm, "end": v(-2165.27, 279.4) * mm});
            skLineSegment(sketch, "E35.25.0.3", {"start": v(-2165.27, 279.4) * mm, "end": v(-2178.13, 279.4) * mm});
            skArc(sketch, "E35.25.0.4", {"start": v(-2178.13, 279.4) * mm, "mid": v(-2188.72, 276.19) * mm, "end": v(-2195.73, 267.64) * mm});
            skLineSegment(sketch, "E35.25.0.5", {"start": v(-2195.73, 267.64) * mm, "end": v(-2201, 254.92) * mm});
            skArc(sketch, "E35.26.0.0", {"start": v(-2218.6, 254.92) * mm, "mid": v(-2209.8, 249.05) * mm, "end": v(-2201, 254.92) * mm});
            skLineSegment(sketch, "E35.26.0.1", {"start": v(-2218.6, 254.92) * mm, "end": v(-2223.87, 267.64) * mm});
            skArc(sketch, "E35.26.0.2", {"start": v(-2223.87, 267.64) * mm, "mid": v(-2230.88, 276.19) * mm, "end": v(-2241.47, 279.4) * mm});
            skLineSegment(sketch, "E35.26.0.3", {"start": v(-2241.47, 279.4) * mm, "end": v(-2254.33, 279.4) * mm});
            skArc(sketch, "E35.26.0.4", {"start": v(-2254.33, 279.4) * mm, "mid": v(-2264.92, 276.19) * mm, "end": v(-2271.93, 267.64) * mm});
            skLineSegment(sketch, "E35.26.0.5", {"start": v(-2271.93, 267.64) * mm, "end": v(-2277.2, 254.92) * mm});
            skArc(sketch, "E35.27.0.0", {"start": v(-2294.8, 254.92) * mm, "mid": v(-2286, 249.05) * mm, "end": v(-2277.2, 254.92) * mm});
            skLineSegment(sketch, "E35.27.0.1", {"start": v(-2294.8, 254.92) * mm, "end": v(-2300.07, 267.64) * mm});
            skArc(sketch, "E35.27.0.2", {"start": v(-2300.07, 267.64) * mm, "mid": v(-2307.08, 276.19) * mm, "end": v(-2317.67, 279.4) * mm});
            skLineSegment(sketch, "E35.27.0.3", {"start": v(-2317.67, 279.4) * mm, "end": v(-2330.53, 279.4) * mm});
            skArc(sketch, "E35.27.0.4", {"start": v(-2330.53, 279.4) * mm, "mid": v(-2341.12, 276.19) * mm, "end": v(-2348.13, 267.64) * mm});
            skLineSegment(sketch, "E35.27.0.5", {"start": v(-2348.13, 267.64) * mm, "end": v(-2353.4, 254.92) * mm});
            skArc(sketch, "E35.28.0.0", {"start": v(-2371, 254.92) * mm, "mid": v(-2362.2, 249.05) * mm, "end": v(-2353.4, 254.92) * mm});
            skLineSegment(sketch, "E35.28.0.1", {"start": v(-2371, 254.92) * mm, "end": v(-2376.27, 267.64) * mm});
            skArc(sketch, "E35.28.0.2", {"start": v(-2376.27, 267.64) * mm, "mid": v(-2383.28, 276.19) * mm, "end": v(-2393.87, 279.4) * mm});
            skLineSegment(sketch, "E35.28.0.3", {"start": v(-2393.87, 279.4) * mm, "end": v(-2406.73, 279.4) * mm});
            skArc(sketch, "E35.28.0.4", {"start": v(-2406.73, 279.4) * mm, "mid": v(-2417.32, 276.19) * mm, "end": v(-2424.33, 267.64) * mm});
            skLineSegment(sketch, "E35.28.0.5", {"start": v(-2424.33, 267.64) * mm, "end": v(-2429.6, 254.92) * mm});
            skArc(sketch, "E35.29.0.0", {"start": v(-2447.2, 254.92) * mm, "mid": v(-2438.4, 249.05) * mm, "end": v(-2429.6, 254.92) * mm});
            skLineSegment(sketch, "E35.29.0.1", {"start": v(-2447.2, 254.92) * mm, "end": v(-2452.47, 267.64) * mm});
            skArc(sketch, "E35.29.0.2", {"start": v(-2452.47, 267.64) * mm, "mid": v(-2459.48, 276.19) * mm, "end": v(-2470.07, 279.4) * mm});
            skLineSegment(sketch, "E35.29.0.3", {"start": v(-2470.07, 279.4) * mm, "end": v(-2482.93, 279.4) * mm});
            skArc(sketch, "E35.29.0.4", {"start": v(-2482.93, 279.4) * mm, "mid": v(-2493.52, 276.19) * mm, "end": v(-2500.53, 267.64) * mm});
            skLineSegment(sketch, "E35.29.0.5", {"start": v(-2500.53, 267.64) * mm, "end": v(-2505.8, 254.92) * mm});
            skArc(sketch, "E35.30.0.0", {"start": v(-2523.4, 254.92) * mm, "mid": v(-2514.6, 249.05) * mm, "end": v(-2505.8, 254.92) * mm});
            skLineSegment(sketch, "E35.30.0.1", {"start": v(-2523.4, 254.92) * mm, "end": v(-2528.67, 267.64) * mm});
            skArc(sketch, "E35.30.0.2", {"start": v(-2528.67, 267.64) * mm, "mid": v(-2535.68, 276.19) * mm, "end": v(-2546.27, 279.4) * mm});
            skLineSegment(sketch, "E35.30.0.3", {"start": v(-2546.27, 279.4) * mm, "end": v(-2559.13, 279.4) * mm});
            skArc(sketch, "E35.30.0.4", {"start": v(-2559.13, 279.4) * mm, "mid": v(-2569.72, 276.19) * mm, "end": v(-2576.73, 267.64) * mm});
            skLineSegment(sketch, "E35.30.0.5", {"start": v(-2576.73, 267.64) * mm, "end": v(-2582, 254.92) * mm});
            skArc(sketch, "E35.31.0.0", {"start": v(-2599.6, 254.92) * mm, "mid": v(-2590.8, 249.05) * mm, "end": v(-2582, 254.92) * mm});
            skLineSegment(sketch, "E35.31.0.1", {"start": v(-2599.6, 254.92) * mm, "end": v(-2604.87, 267.64) * mm});
            skArc(sketch, "E35.31.0.2", {"start": v(-2604.87, 267.64) * mm, "mid": v(-2611.88, 276.19) * mm, "end": v(-2622.47, 279.4) * mm});
            skLineSegment(sketch, "E35.31.0.3", {"start": v(-2622.47, 279.4) * mm, "end": v(-2635.33, 279.4) * mm});
            skArc(sketch, "E35.31.0.4", {"start": v(-2635.33, 279.4) * mm, "mid": v(-2645.92, 276.19) * mm, "end": v(-2652.93, 267.64) * mm});
            skLineSegment(sketch, "E35.31.0.5", {"start": v(-2652.93, 267.64) * mm, "end": v(-2658.2, 254.92) * mm});
            skArc(sketch, "E35.32.0.0", {"start": v(-2675.8, 254.92) * mm, "mid": v(-2667, 249.05) * mm, "end": v(-2658.2, 254.92) * mm});
            skLineSegment(sketch, "E35.32.0.1", {"start": v(-2675.8, 254.92) * mm, "end": v(-2681.07, 267.64) * mm});
            skArc(sketch, "E35.32.0.2", {"start": v(-2681.07, 267.64) * mm, "mid": v(-2688.08, 276.19) * mm, "end": v(-2698.67, 279.4) * mm});
            skLineSegment(sketch, "E35.32.0.3", {"start": v(-2698.67, 279.4) * mm, "end": v(-2711.53, 279.4) * mm});
            skArc(sketch, "E35.32.0.4", {"start": v(-2711.53, 279.4) * mm, "mid": v(-2722.12, 276.19) * mm, "end": v(-2729.13, 267.64) * mm});
            skLineSegment(sketch, "E35.32.0.5", {"start": v(-2729.13, 267.64) * mm, "end": v(-2734.4, 254.92) * mm});
            skArc(sketch, "E35.33.0.0", {"start": v(-2752, 254.92) * mm, "mid": v(-2743.2, 249.05) * mm, "end": v(-2734.4, 254.92) * mm});
            skLineSegment(sketch, "E35.33.0.1", {"start": v(-2752, 254.92) * mm, "end": v(-2757.27, 267.64) * mm});
            skArc(sketch, "E35.33.0.2", {"start": v(-2757.27, 267.64) * mm, "mid": v(-2764.28, 276.19) * mm, "end": v(-2774.87, 279.4) * mm});
            skLineSegment(sketch, "E35.33.0.3", {"start": v(-2774.87, 279.4) * mm, "end": v(-2787.73, 279.4) * mm});
            skArc(sketch, "E35.33.0.4", {"start": v(-2787.73, 279.4) * mm, "mid": v(-2798.32, 276.19) * mm, "end": v(-2805.33, 267.64) * mm});
            skLineSegment(sketch, "E35.33.0.5", {"start": v(-2805.33, 267.64) * mm, "end": v(-2810.6, 254.92) * mm});
            skArc(sketch, "E35.34.0.0", {"start": v(-2828.2, 254.92) * mm, "mid": v(-2819.4, 249.05) * mm, "end": v(-2810.6, 254.92) * mm});
            skLineSegment(sketch, "E35.34.0.1", {"start": v(-2828.2, 254.92) * mm, "end": v(-2833.47, 267.64) * mm});
            skArc(sketch, "E35.34.0.2", {"start": v(-2833.47, 267.64) * mm, "mid": v(-2840.48, 276.19) * mm, "end": v(-2851.07, 279.4) * mm});
            skLineSegment(sketch, "E35.34.0.3", {"start": v(-2851.07, 279.4) * mm, "end": v(-2863.93, 279.4) * mm});
            skArc(sketch, "E35.34.0.4", {"start": v(-2863.93, 279.4) * mm, "mid": v(-2874.52, 276.19) * mm, "end": v(-2881.53, 267.64) * mm});
            skLineSegment(sketch, "E35.34.0.5", {"start": v(-2881.53, 267.64) * mm, "end": v(-2886.8, 254.92) * mm});
            skArc(sketch, "E35.35.0.0", {"start": v(-2904.4, 254.92) * mm, "mid": v(-2895.6, 249.05) * mm, "end": v(-2886.8, 254.92) * mm});
            skLineSegment(sketch, "E35.35.0.1", {"start": v(-2904.4, 254.92) * mm, "end": v(-2909.67, 267.64) * mm});
            skArc(sketch, "E35.35.0.2", {"start": v(-2909.67, 267.64) * mm, "mid": v(-2916.68, 276.19) * mm, "end": v(-2927.27, 279.4) * mm});
            skLineSegment(sketch, "E35.35.0.3", {"start": v(-2927.27, 279.4) * mm, "end": v(-2940.13, 279.4) * mm});
            skArc(sketch, "E35.35.0.4", {"start": v(-2940.13, 279.4) * mm, "mid": v(-2950.72, 276.19) * mm, "end": v(-2957.73, 267.64) * mm});
            skLineSegment(sketch, "E35.35.0.5", {"start": v(-2957.73, 267.64) * mm, "end": v(-2963, 254.92) * mm});
            skArc(sketch, "E35.36.0.0", {"start": v(-2980.6, 254.92) * mm, "mid": v(-2971.8, 249.05) * mm, "end": v(-2963, 254.92) * mm});
            skLineSegment(sketch, "E35.36.0.1", {"start": v(-2980.6, 254.92) * mm, "end": v(-2985.87, 267.64) * mm});
            skArc(sketch, "E35.36.0.2", {"start": v(-2985.87, 267.64) * mm, "mid": v(-2992.88, 276.19) * mm, "end": v(-3003.47, 279.4) * mm});
            skLineSegment(sketch, "E35.36.0.3", {"start": v(-3003.47, 279.4) * mm, "end": v(-3016.33, 279.4) * mm});
            skArc(sketch, "E35.36.0.4", {"start": v(-3016.33, 279.4) * mm, "mid": v(-3026.92, 276.19) * mm, "end": v(-3033.93, 267.64) * mm});
            skLineSegment(sketch, "E35.36.0.5", {"start": v(-3033.93, 267.64) * mm, "end": v(-3039.2, 254.92) * mm});
            skArc(sketch, "E35.37.0.0", {"start": v(-3056.8, 254.92) * mm, "mid": v(-3048, 249.05) * mm, "end": v(-3039.2, 254.92) * mm});
            skLineSegment(sketch, "E35.37.0.1", {"start": v(-3056.8, 254.92) * mm, "end": v(-3062.07, 267.64) * mm});
            skArc(sketch, "E35.37.0.2", {"start": v(-3062.07, 267.64) * mm, "mid": v(-3069.08, 276.19) * mm, "end": v(-3079.67, 279.4) * mm});
            skLineSegment(sketch, "E35.37.0.3", {"start": v(-3079.67, 279.4) * mm, "end": v(-3092.53, 279.4) * mm});
            skArc(sketch, "E35.37.0.4", {"start": v(-3092.53, 279.4) * mm, "mid": v(-3103.12, 276.19) * mm, "end": v(-3110.13, 267.64) * mm});
            skLineSegment(sketch, "E35.37.0.5", {"start": v(-3110.13, 267.64) * mm, "end": v(-3115.4, 254.92) * mm});
            skArc(sketch, "E35.38.0.0", {"start": v(-3133, 254.92) * mm, "mid": v(-3124.2, 249.05) * mm, "end": v(-3115.4, 254.92) * mm});
            skLineSegment(sketch, "E35.38.0.1", {"start": v(-3133, 254.92) * mm, "end": v(-3138.27, 267.64) * mm});
            skArc(sketch, "E35.38.0.2", {"start": v(-3138.27, 267.64) * mm, "mid": v(-3145.28, 276.19) * mm, "end": v(-3155.87, 279.4) * mm});
            skLineSegment(sketch, "E35.38.0.3", {"start": v(-3155.87, 279.4) * mm, "end": v(-3168.73, 279.4) * mm});
            skArc(sketch, "E35.38.0.4", {"start": v(-3168.73, 279.4) * mm, "mid": v(-3179.32, 276.19) * mm, "end": v(-3186.33, 267.64) * mm});
            skLineSegment(sketch, "E35.38.0.5", {"start": v(-3186.33, 267.64) * mm, "end": v(-3191.6, 254.92) * mm});
            skArc(sketch, "E35.39.0.0", {"start": v(-3209.2, 254.92) * mm, "mid": v(-3200.4, 249.05) * mm, "end": v(-3191.6, 254.92) * mm});
            skLineSegment(sketch, "E35.39.0.1", {"start": v(-3209.2, 254.92) * mm, "end": v(-3214.47, 267.64) * mm});
            skArc(sketch, "E35.39.0.2", {"start": v(-3214.47, 267.64) * mm, "mid": v(-3221.48, 276.19) * mm, "end": v(-3232.07, 279.4) * mm});
            skLineSegment(sketch, "E35.39.0.3", {"start": v(-3232.07, 279.4) * mm, "end": v(-3244.93, 279.4) * mm});
            skArc(sketch, "E35.39.0.4", {"start": v(-3244.93, 279.4) * mm, "mid": v(-3255.52, 276.19) * mm, "end": v(-3262.53, 267.64) * mm});
            skLineSegment(sketch, "E35.39.0.5", {"start": v(-3262.53, 267.64) * mm, "end": v(-3267.8, 254.92) * mm});
            skArc(sketch, "E35.40.0.0", {"start": v(-3285.4, 254.92) * mm, "mid": v(-3276.6, 249.05) * mm, "end": v(-3267.8, 254.92) * mm});
            skLineSegment(sketch, "E35.40.0.1", {"start": v(-3285.4, 254.92) * mm, "end": v(-3290.67, 267.64) * mm});
            skArc(sketch, "E35.40.0.2", {"start": v(-3290.67, 267.64) * mm, "mid": v(-3297.68, 276.19) * mm, "end": v(-3308.27, 279.4) * mm});
            skLineSegment(sketch, "E35.40.0.3", {"start": v(-3308.27, 279.4) * mm, "end": v(-3321.13, 279.4) * mm});
            skArc(sketch, "E35.40.0.4", {"start": v(-3321.13, 279.4) * mm, "mid": v(-3331.72, 276.19) * mm, "end": v(-3338.73, 267.64) * mm});
            skLineSegment(sketch, "E35.40.0.5", {"start": v(-3338.73, 267.64) * mm, "end": v(-3344, 254.92) * mm});
            skArc(sketch, "E35.41.0.0", {"start": v(-3361.6, 254.92) * mm, "mid": v(-3352.8, 249.05) * mm, "end": v(-3344, 254.92) * mm});
            skLineSegment(sketch, "E35.41.0.1", {"start": v(-3361.6, 254.92) * mm, "end": v(-3366.87, 267.64) * mm});
            skArc(sketch, "E35.41.0.2", {"start": v(-3366.87, 267.64) * mm, "mid": v(-3373.88, 276.19) * mm, "end": v(-3384.47, 279.4) * mm});
            skLineSegment(sketch, "E35.41.0.3", {"start": v(-3384.47, 279.4) * mm, "end": v(-3397.33, 279.4) * mm});
            skArc(sketch, "E35.41.0.4", {"start": v(-3397.33, 279.4) * mm, "mid": v(-3407.92, 276.19) * mm, "end": v(-3414.93, 267.64) * mm});
            skLineSegment(sketch, "E35.41.0.5", {"start": v(-3414.93, 267.64) * mm, "end": v(-3420.2, 254.92) * mm});
            skArc(sketch, "E35.42.0.0", {"start": v(-3437.8, 254.92) * mm, "mid": v(-3429, 249.05) * mm, "end": v(-3420.2, 254.92) * mm});
            skLineSegment(sketch, "E35.42.0.1", {"start": v(-3437.8, 254.92) * mm, "end": v(-3443.07, 267.64) * mm});
            skArc(sketch, "E35.42.0.2", {"start": v(-3443.07, 267.64) * mm, "mid": v(-3450.08, 276.19) * mm, "end": v(-3460.67, 279.4) * mm});
            skLineSegment(sketch, "E35.42.0.3", {"start": v(-3460.67, 279.4) * mm, "end": v(-3473.53, 279.4) * mm});
            skArc(sketch, "E35.42.0.4", {"start": v(-3473.53, 279.4) * mm, "mid": v(-3484.12, 276.19) * mm, "end": v(-3491.13, 267.64) * mm});
            skLineSegment(sketch, "E35.42.0.5", {"start": v(-3491.13, 267.64) * mm, "end": v(-3496.4, 254.92) * mm});
            skArc(sketch, "E35.43.0.0", {"start": v(-3514, 254.92) * mm, "mid": v(-3505.2, 249.05) * mm, "end": v(-3496.4, 254.92) * mm});
            skLineSegment(sketch, "E35.43.0.1", {"start": v(-3514, 254.92) * mm, "end": v(-3519.27, 267.64) * mm});
            skArc(sketch, "E35.43.0.2", {"start": v(-3519.27, 267.64) * mm, "mid": v(-3526.28, 276.19) * mm, "end": v(-3536.87, 279.4) * mm});
            skLineSegment(sketch, "E35.43.0.3", {"start": v(-3536.87, 279.4) * mm, "end": v(-3549.73, 279.4) * mm});
            skArc(sketch, "E35.43.0.4", {"start": v(-3549.73, 279.4) * mm, "mid": v(-3560.32, 276.19) * mm, "end": v(-3567.33, 267.64) * mm});
            skLineSegment(sketch, "E35.43.0.5", {"start": v(-3567.33, 267.64) * mm, "end": v(-3572.6, 254.92) * mm});
            skArc(sketch, "E35.44.0.0", {"start": v(-3590.2, 254.92) * mm, "mid": v(-3581.4, 249.05) * mm, "end": v(-3572.6, 254.92) * mm});
            skLineSegment(sketch, "E35.44.0.1", {"start": v(-3590.2, 254.92) * mm, "end": v(-3595.47, 267.64) * mm});
            skArc(sketch, "E35.44.0.2", {"start": v(-3595.47, 267.64) * mm, "mid": v(-3602.48, 276.19) * mm, "end": v(-3613.07, 279.4) * mm});
            skLineSegment(sketch, "E35.44.0.3", {"start": v(-3613.07, 279.4) * mm, "end": v(-3625.93, 279.4) * mm});
            skArc(sketch, "E35.44.0.4", {"start": v(-3625.93, 279.4) * mm, "mid": v(-3636.52, 276.19) * mm, "end": v(-3643.53, 267.64) * mm});
            skLineSegment(sketch, "E35.44.0.5", {"start": v(-3643.53, 267.64) * mm, "end": v(-3648.8, 254.92) * mm});
            skArc(sketch, "E35.45.0.0", {"start": v(-3666.4, 254.92) * mm, "mid": v(-3657.6, 249.05) * mm, "end": v(-3648.8, 254.92) * mm});
            skLineSegment(sketch, "E35.45.0.1", {"start": v(-3666.4, 254.92) * mm, "end": v(-3671.67, 267.64) * mm});
            skArc(sketch, "E35.45.0.2", {"start": v(-3671.67, 267.64) * mm, "mid": v(-3678.68, 276.19) * mm, "end": v(-3689.27, 279.4) * mm});
            skLineSegment(sketch, "E35.45.0.3", {"start": v(-3689.27, 279.4) * mm, "end": v(-3702.13, 279.4) * mm});
            skArc(sketch, "E35.45.0.4", {"start": v(-3702.13, 279.4) * mm, "mid": v(-3712.72, 276.19) * mm, "end": v(-3719.73, 267.64) * mm});
            skLineSegment(sketch, "E35.45.0.5", {"start": v(-3719.73, 267.64) * mm, "end": v(-3725, 254.92) * mm});
            skArc(sketch, "E35.46.0.0", {"start": v(-3742.6, 254.92) * mm, "mid": v(-3733.8, 249.05) * mm, "end": v(-3725, 254.92) * mm});
            skLineSegment(sketch, "E35.46.0.1", {"start": v(-3742.6, 254.92) * mm, "end": v(-3747.87, 267.64) * mm});
            skArc(sketch, "E35.46.0.2", {"start": v(-3747.87, 267.64) * mm, "mid": v(-3754.88, 276.19) * mm, "end": v(-3765.47, 279.4) * mm});
            skLineSegment(sketch, "E35.46.0.3", {"start": v(-3765.47, 279.4) * mm, "end": v(-3778.33, 279.4) * mm});
            skArc(sketch, "E35.46.0.4", {"start": v(-3778.33, 279.4) * mm, "mid": v(-3788.92, 276.19) * mm, "end": v(-3795.93, 267.64) * mm});
            skLineSegment(sketch, "E35.46.0.5", {"start": v(-3795.93, 267.64) * mm, "end": v(-3801.2, 254.92) * mm});
            skArc(sketch, "E35.47.0.0", {"start": v(-3818.8, 254.92) * mm, "mid": v(-3810, 249.05) * mm, "end": v(-3801.2, 254.92) * mm});
            skLineSegment(sketch, "E35.47.0.1", {"start": v(-3818.8, 254.92) * mm, "end": v(-3824.07, 267.64) * mm});
            skArc(sketch, "E35.47.0.2", {"start": v(-3824.07, 267.64) * mm, "mid": v(-3831.08, 276.19) * mm, "end": v(-3841.67, 279.4) * mm});
            skLineSegment(sketch, "E35.47.0.3", {"start": v(-3841.67, 279.4) * mm, "end": v(-3854.53, 279.4) * mm});
            skArc(sketch, "E35.47.0.4", {"start": v(-3854.53, 279.4) * mm, "mid": v(-3865.12, 276.19) * mm, "end": v(-3872.13, 267.64) * mm});
            skLineSegment(sketch, "E35.47.0.5", {"start": v(-3872.13, 267.64) * mm, "end": v(-3877.4, 254.92) * mm});
            skArc(sketch, "E35.48.0.0", {"start": v(-3895, 254.92) * mm, "mid": v(-3886.2, 249.05) * mm, "end": v(-3877.4, 254.92) * mm});
            skLineSegment(sketch, "E35.48.0.1", {"start": v(-3895, 254.92) * mm, "end": v(-3900.27, 267.64) * mm});
            skArc(sketch, "E35.48.0.2", {"start": v(-3900.27, 267.64) * mm, "mid": v(-3907.28, 276.19) * mm, "end": v(-3917.87, 279.4) * mm});
            skLineSegment(sketch, "E35.48.0.3", {"start": v(-3917.87, 279.4) * mm, "end": v(-3930.73, 279.4) * mm});
            skArc(sketch, "E35.48.0.4", {"start": v(-3930.73, 279.4) * mm, "mid": v(-3941.32, 276.19) * mm, "end": v(-3948.33, 267.64) * mm});
            skLineSegment(sketch, "E35.48.0.5", {"start": v(-3948.33, 267.64) * mm, "end": v(-3953.6, 254.92) * mm});
            skArc(sketch, "E35.49.0.0", {"start": v(-3971.2, 254.92) * mm, "mid": v(-3962.4, 249.05) * mm, "end": v(-3953.6, 254.92) * mm});
            skLineSegment(sketch, "E35.49.0.1", {"start": v(-3971.2, 254.92) * mm, "end": v(-3976.47, 267.64) * mm});
            skArc(sketch, "E35.49.0.2", {"start": v(-3976.47, 267.64) * mm, "mid": v(-3983.48, 276.19) * mm, "end": v(-3994.07, 279.4) * mm});
            skLineSegment(sketch, "E35.49.0.3", {"start": v(-3994.07, 279.4) * mm, "end": v(-4006.93, 279.4) * mm});
            skArc(sketch, "E35.49.0.4", {"start": v(-4006.93, 279.4) * mm, "mid": v(-4017.52, 276.19) * mm, "end": v(-4024.53, 267.64) * mm});
            skLineSegment(sketch, "E35.49.0.5", {"start": v(-4024.53, 267.64) * mm, "end": v(-4029.8, 254.92) * mm});
            skArc(sketch, "E35.50.0.0", {"start": v(-4047.4, 254.92) * mm, "mid": v(-4038.6, 249.05) * mm, "end": v(-4029.8, 254.92) * mm});
            skLineSegment(sketch, "E35.50.0.1", {"start": v(-4047.4, 254.92) * mm, "end": v(-4052.67, 267.64) * mm});
            skArc(sketch, "E35.50.0.2", {"start": v(-4052.67, 267.64) * mm, "mid": v(-4059.68, 276.19) * mm, "end": v(-4070.27, 279.4) * mm});
            skLineSegment(sketch, "E35.50.0.3", {"start": v(-4070.27, 279.4) * mm, "end": v(-4083.13, 279.4) * mm});
            skArc(sketch, "E35.50.0.4", {"start": v(-4083.13, 279.4) * mm, "mid": v(-4093.72, 276.19) * mm, "end": v(-4100.73, 267.64) * mm});
            skLineSegment(sketch, "E35.50.0.5", {"start": v(-4100.73, 267.64) * mm, "end": v(-4106, 254.92) * mm});
            skArc(sketch, "E35.51.0.0", {"start": v(-4123.6, 254.92) * mm, "mid": v(-4114.8, 249.05) * mm, "end": v(-4106, 254.92) * mm});
            skLineSegment(sketch, "E35.51.0.1", {"start": v(-4123.6, 254.92) * mm, "end": v(-4128.87, 267.64) * mm});
            skArc(sketch, "E35.51.0.2", {"start": v(-4128.87, 267.64) * mm, "mid": v(-4135.88, 276.19) * mm, "end": v(-4146.47, 279.4) * mm});
            skLineSegment(sketch, "E35.51.0.3", {"start": v(-4146.47, 279.4) * mm, "end": v(-4159.33, 279.4) * mm});
            skArc(sketch, "E35.51.0.4", {"start": v(-4159.33, 279.4) * mm, "mid": v(-4169.92, 276.19) * mm, "end": v(-4176.93, 267.64) * mm});
            skLineSegment(sketch, "E35.51.0.5", {"start": v(-4176.93, 267.64) * mm, "end": v(-4182.2, 254.92) * mm});
            skArc(sketch, "E35.52.0.0", {"start": v(-4199.8, 254.92) * mm, "mid": v(-4191, 249.05) * mm, "end": v(-4182.2, 254.92) * mm});
            skLineSegment(sketch, "E35.52.0.1", {"start": v(-4199.8, 254.92) * mm, "end": v(-4205.07, 267.64) * mm});
            skArc(sketch, "E35.52.0.2", {"start": v(-4205.07, 267.64) * mm, "mid": v(-4212.08, 276.19) * mm, "end": v(-4222.67, 279.4) * mm});
            skLineSegment(sketch, "E35.52.0.3", {"start": v(-4222.67, 279.4) * mm, "end": v(-4235.53, 279.4) * mm});
            skArc(sketch, "E35.52.0.4", {"start": v(-4235.53, 279.4) * mm, "mid": v(-4246.12, 276.19) * mm, "end": v(-4253.13, 267.64) * mm});
            skLineSegment(sketch, "E35.52.0.5", {"start": v(-4253.13, 267.64) * mm, "end": v(-4258.4, 254.92) * mm});
            skArc(sketch, "E35.53.0.0", {"start": v(-4276, 254.92) * mm, "mid": v(-4267.2, 249.05) * mm, "end": v(-4258.4, 254.92) * mm});
            skLineSegment(sketch, "E35.53.0.1", {"start": v(-4276, 254.92) * mm, "end": v(-4281.27, 267.64) * mm});
            skArc(sketch, "E35.53.0.2", {"start": v(-4281.27, 267.64) * mm, "mid": v(-4288.28, 276.19) * mm, "end": v(-4298.87, 279.4) * mm});
            skLineSegment(sketch, "E35.53.0.3", {"start": v(-4298.87, 279.4) * mm, "end": v(-4311.73, 279.4) * mm});
            skArc(sketch, "E35.53.0.4", {"start": v(-4311.73, 279.4) * mm, "mid": v(-4322.32, 276.19) * mm, "end": v(-4329.33, 267.64) * mm});
            skLineSegment(sketch, "E35.53.0.5", {"start": v(-4329.33, 267.64) * mm, "end": v(-4334.6, 254.92) * mm});
            skArc(sketch, "E35.54.0.0", {"start": v(-4352.2, 254.92) * mm, "mid": v(-4343.4, 249.05) * mm, "end": v(-4334.6, 254.92) * mm});
            skLineSegment(sketch, "E35.54.0.1", {"start": v(-4352.2, 254.92) * mm, "end": v(-4357.47, 267.64) * mm});
            skArc(sketch, "E35.54.0.2", {"start": v(-4357.47, 267.64) * mm, "mid": v(-4364.48, 276.19) * mm, "end": v(-4375.07, 279.4) * mm});
            skLineSegment(sketch, "E35.54.0.3", {"start": v(-4375.07, 279.4) * mm, "end": v(-4387.93, 279.4) * mm});
            skArc(sketch, "E35.54.0.4", {"start": v(-4387.93, 279.4) * mm, "mid": v(-4398.52, 276.19) * mm, "end": v(-4405.53, 267.64) * mm});
            skLineSegment(sketch, "E35.54.0.5", {"start": v(-4405.53, 267.64) * mm, "end": v(-4410.8, 254.92) * mm});
            skArc(sketch, "E35.55.0.0", {"start": v(-4428.4, 254.92) * mm, "mid": v(-4419.6, 249.05) * mm, "end": v(-4410.8, 254.92) * mm});
            skLineSegment(sketch, "E35.55.0.1", {"start": v(-4428.4, 254.92) * mm, "end": v(-4433.67, 267.64) * mm});
            skArc(sketch, "E35.55.0.2", {"start": v(-4433.67, 267.64) * mm, "mid": v(-4440.68, 276.19) * mm, "end": v(-4451.27, 279.4) * mm});
            skLineSegment(sketch, "E35.55.0.3", {"start": v(-4451.27, 279.4) * mm, "end": v(-4464.13, 279.4) * mm});
            skArc(sketch, "E35.55.0.4", {"start": v(-4464.13, 279.4) * mm, "mid": v(-4474.72, 276.19) * mm, "end": v(-4481.73, 267.64) * mm});
            skLineSegment(sketch, "E35.55.0.5", {"start": v(-4481.73, 267.64) * mm, "end": v(-4487, 254.92) * mm});
            skArc(sketch, "E35.56.0.0", {"start": v(-4504.6, 254.92) * mm, "mid": v(-4495.8, 249.05) * mm, "end": v(-4487, 254.92) * mm});
            skLineSegment(sketch, "E35.56.0.1", {"start": v(-4504.6, 254.92) * mm, "end": v(-4509.87, 267.64) * mm});
            skArc(sketch, "E35.56.0.2", {"start": v(-4509.87, 267.64) * mm, "mid": v(-4516.88, 276.19) * mm, "end": v(-4527.47, 279.4) * mm});
            skLineSegment(sketch, "E35.56.0.3", {"start": v(-4527.47, 279.4) * mm, "end": v(-4540.33, 279.4) * mm});
            skArc(sketch, "E35.56.0.4", {"start": v(-4540.33, 279.4) * mm, "mid": v(-4550.92, 276.19) * mm, "end": v(-4557.93, 267.64) * mm});
            skLineSegment(sketch, "E35.56.0.5", {"start": v(-4557.93, 267.64) * mm, "end": v(-4563.2, 254.92) * mm});
            skArc(sketch, "E35.57.0.0", {"start": v(-4580.8, 254.92) * mm, "mid": v(-4572, 249.05) * mm, "end": v(-4563.2, 254.92) * mm});
            skLineSegment(sketch, "E35.57.0.1", {"start": v(-4580.8, 254.92) * mm, "end": v(-4586.07, 267.64) * mm});
            skArc(sketch, "E35.57.0.2", {"start": v(-4586.07, 267.64) * mm, "mid": v(-4593.08, 276.19) * mm, "end": v(-4603.67, 279.4) * mm});
            skLineSegment(sketch, "E35.57.0.3", {"start": v(-4603.67, 279.4) * mm, "end": v(-4616.53, 279.4) * mm});
            skArc(sketch, "E35.57.0.4", {"start": v(-4616.53, 279.4) * mm, "mid": v(-4627.12, 276.19) * mm, "end": v(-4634.13, 267.64) * mm});
            skLineSegment(sketch, "E35.57.0.5", {"start": v(-4634.13, 267.64) * mm, "end": v(-4639.4, 254.92) * mm});
            skArc(sketch, "E35.58.0.0", {"start": v(-4657, 254.92) * mm, "mid": v(-4648.2, 249.05) * mm, "end": v(-4639.4, 254.92) * mm});
            skLineSegment(sketch, "E35.58.0.1", {"start": v(-4657, 254.92) * mm, "end": v(-4662.27, 267.64) * mm});
            skArc(sketch, "E35.58.0.2", {"start": v(-4662.27, 267.64) * mm, "mid": v(-4669.28, 276.19) * mm, "end": v(-4679.87, 279.4) * mm});
            skLineSegment(sketch, "E35.58.0.3", {"start": v(-4679.87, 279.4) * mm, "end": v(-4692.73, 279.4) * mm});
            skArc(sketch, "E35.58.0.4", {"start": v(-4692.73, 279.4) * mm, "mid": v(-4703.32, 276.19) * mm, "end": v(-4710.33, 267.64) * mm});
            skLineSegment(sketch, "E35.58.0.5", {"start": v(-4710.33, 267.64) * mm, "end": v(-4715.6, 254.92) * mm});
            skArc(sketch, "E35.59.0.0", {"start": v(-4733.2, 254.92) * mm, "mid": v(-4724.4, 249.05) * mm, "end": v(-4715.6, 254.92) * mm});
            skLineSegment(sketch, "E35.59.0.1", {"start": v(-4733.2, 254.92) * mm, "end": v(-4738.47, 267.64) * mm});
            skArc(sketch, "E35.59.0.2", {"start": v(-4738.47, 267.64) * mm, "mid": v(-4745.48, 276.19) * mm, "end": v(-4756.07, 279.4) * mm});
            skLineSegment(sketch, "E35.59.0.3", {"start": v(-4756.07, 279.4) * mm, "end": v(-4768.93, 279.4) * mm});
            skArc(sketch, "E35.59.0.4", {"start": v(-4768.93, 279.4) * mm, "mid": v(-4779.52, 276.19) * mm, "end": v(-4786.53, 267.64) * mm});
            skLineSegment(sketch, "E35.59.0.5", {"start": v(-4786.53, 267.64) * mm, "end": v(-4791.8, 254.92) * mm});
            skArc(sketch, "E35.60.0.0", {"start": v(-4809.4, 254.92) * mm, "mid": v(-4800.6, 249.05) * mm, "end": v(-4791.8, 254.92) * mm});
            skLineSegment(sketch, "E35.60.0.1", {"start": v(-4809.4, 254.92) * mm, "end": v(-4814.67, 267.64) * mm});
            skArc(sketch, "E35.60.0.2", {"start": v(-4814.67, 267.64) * mm, "mid": v(-4821.68, 276.19) * mm, "end": v(-4832.27, 279.4) * mm});
            skLineSegment(sketch, "E35.60.0.3", {"start": v(-4832.27, 279.4) * mm, "end": v(-4845.13, 279.4) * mm});
            skArc(sketch, "E35.60.0.4", {"start": v(-4845.13, 279.4) * mm, "mid": v(-4855.72, 276.19) * mm, "end": v(-4862.73, 267.64) * mm});
            skLineSegment(sketch, "E35.60.0.5", {"start": v(-4862.73, 267.64) * mm, "end": v(-4868, 254.92) * mm});
            skArc(sketch, "E35.61.0.0", {"start": v(-4885.6, 254.92) * mm, "mid": v(-4876.8, 249.05) * mm, "end": v(-4868, 254.92) * mm});
            skLineSegment(sketch, "E35.61.0.1", {"start": v(-4885.6, 254.92) * mm, "end": v(-4890.87, 267.64) * mm});
            skArc(sketch, "E35.61.0.2", {"start": v(-4890.87, 267.64) * mm, "mid": v(-4897.88, 276.19) * mm, "end": v(-4908.47, 279.4) * mm});
            skLineSegment(sketch, "E35.61.0.3", {"start": v(-4908.47, 279.4) * mm, "end": v(-4921.33, 279.4) * mm});
            skArc(sketch, "E35.61.0.4", {"start": v(-4921.33, 279.4) * mm, "mid": v(-4931.92, 276.19) * mm, "end": v(-4938.93, 267.64) * mm});
            skLineSegment(sketch, "E35.61.0.5", {"start": v(-4938.93, 267.64) * mm, "end": v(-4944.2, 254.92) * mm});
            skArc(sketch, "E35.62.0.0", {"start": v(-4961.8, 254.92) * mm, "mid": v(-4953, 249.05) * mm, "end": v(-4944.2, 254.92) * mm});
            skLineSegment(sketch, "E35.62.0.1", {"start": v(-4961.8, 254.92) * mm, "end": v(-4967.07, 267.64) * mm});
            skArc(sketch, "E35.62.0.2", {"start": v(-4967.07, 267.64) * mm, "mid": v(-4974.08, 276.19) * mm, "end": v(-4984.67, 279.4) * mm});
            skLineSegment(sketch, "E35.62.0.3", {"start": v(-4984.67, 279.4) * mm, "end": v(-4997.53, 279.4) * mm});
            skArc(sketch, "E35.62.0.4", {"start": v(-4997.53, 279.4) * mm, "mid": v(-5008.12, 276.19) * mm, "end": v(-5015.13, 267.64) * mm});
            skLineSegment(sketch, "E35.62.0.5", {"start": v(-5015.13, 267.64) * mm, "end": v(-5020.4, 254.92) * mm});
            skArc(sketch, "E35.63.0.0", {"start": v(-5038, 254.92) * mm, "mid": v(-5029.2, 249.05) * mm, "end": v(-5020.4, 254.92) * mm});
            skLineSegment(sketch, "E35.63.0.1", {"start": v(-5038, 254.92) * mm, "end": v(-5043.27, 267.64) * mm});
            skArc(sketch, "E35.63.0.2", {"start": v(-5043.27, 267.64) * mm, "mid": v(-5050.28, 276.19) * mm, "end": v(-5060.87, 279.4) * mm});
            skLineSegment(sketch, "E35.63.0.3", {"start": v(-5060.87, 279.4) * mm, "end": v(-5073.73, 279.4) * mm});
            skArc(sketch, "E35.63.0.4", {"start": v(-5073.73, 279.4) * mm, "mid": v(-5084.32, 276.19) * mm, "end": v(-5091.33, 267.64) * mm});
            skLineSegment(sketch, "E35.63.0.5", {"start": v(-5091.33, 267.64) * mm, "end": v(-5096.6, 254.92) * mm});
            skArc(sketch, "E35.64.0.0", {"start": v(-5114.2, 254.92) * mm, "mid": v(-5105.4, 249.05) * mm, "end": v(-5096.6, 254.92) * mm});
            skLineSegment(sketch, "E35.64.0.1", {"start": v(-5114.2, 254.92) * mm, "end": v(-5119.47, 267.64) * mm});
            skArc(sketch, "E35.64.0.2", {"start": v(-5119.47, 267.64) * mm, "mid": v(-5126.48, 276.19) * mm, "end": v(-5137.07, 279.4) * mm});
            skLineSegment(sketch, "E35.64.0.3", {"start": v(-5137.07, 279.4) * mm, "end": v(-5149.93, 279.4) * mm});
            skArc(sketch, "E35.64.0.4", {"start": v(-5149.93, 279.4) * mm, "mid": v(-5160.52, 276.19) * mm, "end": v(-5167.53, 267.64) * mm});
            skLineSegment(sketch, "E35.64.0.5", {"start": v(-5167.53, 267.64) * mm, "end": v(-5172.8, 254.92) * mm});
            skArc(sketch, "E35.65.0.0", {"start": v(-5190.4, 254.92) * mm, "mid": v(-5181.6, 249.05) * mm, "end": v(-5172.8, 254.92) * mm});
            skLineSegment(sketch, "E35.65.0.1", {"start": v(-5190.4, 254.92) * mm, "end": v(-5195.67, 267.64) * mm});
            skArc(sketch, "E35.65.0.2", {"start": v(-5195.67, 267.64) * mm, "mid": v(-5202.68, 276.19) * mm, "end": v(-5213.27, 279.4) * mm});
            skLineSegment(sketch, "E35.65.0.3", {"start": v(-5213.27, 279.4) * mm, "end": v(-5226.13, 279.4) * mm});
            skArc(sketch, "E35.65.0.4", {"start": v(-5226.13, 279.4) * mm, "mid": v(-5236.72, 276.19) * mm, "end": v(-5243.73, 267.64) * mm});
            skLineSegment(sketch, "E35.65.0.5", {"start": v(-5243.73, 267.64) * mm, "end": v(-5249, 254.92) * mm});
            skArc(sketch, "E35.66.0.0", {"start": v(-5266.6, 254.92) * mm, "mid": v(-5257.8, 249.05) * mm, "end": v(-5249, 254.92) * mm});
            skLineSegment(sketch, "E35.66.0.1", {"start": v(-5266.6, 254.92) * mm, "end": v(-5271.87, 267.64) * mm});
            skArc(sketch, "E35.66.0.2", {"start": v(-5271.87, 267.64) * mm, "mid": v(-5278.88, 276.19) * mm, "end": v(-5289.47, 279.4) * mm});
            skLineSegment(sketch, "E35.66.0.3", {"start": v(-5289.47, 279.4) * mm, "end": v(-5302.33, 279.4) * mm});
            skArc(sketch, "E35.66.0.4", {"start": v(-5302.33, 279.4) * mm, "mid": v(-5312.92, 276.19) * mm, "end": v(-5319.93, 267.64) * mm});
            skLineSegment(sketch, "E35.66.0.5", {"start": v(-5319.93, 267.64) * mm, "end": v(-5325.2, 254.92) * mm});
            skArc(sketch, "E35.67.0.0", {"start": v(-5342.8, 254.92) * mm, "mid": v(-5334, 249.05) * mm, "end": v(-5325.2, 254.92) * mm});
            skLineSegment(sketch, "E35.67.0.1", {"start": v(-5342.8, 254.92) * mm, "end": v(-5348.07, 267.64) * mm});
            skArc(sketch, "E35.67.0.2", {"start": v(-5348.07, 267.64) * mm, "mid": v(-5355.08, 276.19) * mm, "end": v(-5365.67, 279.4) * mm});
            skLineSegment(sketch, "E35.67.0.3", {"start": v(-5365.67, 279.4) * mm, "end": v(-5378.53, 279.4) * mm});
            skArc(sketch, "E35.67.0.4", {"start": v(-5378.53, 279.4) * mm, "mid": v(-5389.12, 276.19) * mm, "end": v(-5396.13, 267.64) * mm});
            skLineSegment(sketch, "E35.67.0.5", {"start": v(-5396.13, 267.64) * mm, "end": v(-5401.4, 254.92) * mm});
            skArc(sketch, "E35.68.0.0", {"start": v(-5419, 254.92) * mm, "mid": v(-5410.2, 249.05) * mm, "end": v(-5401.4, 254.92) * mm});
            skLineSegment(sketch, "E35.68.0.1", {"start": v(-5419, 254.92) * mm, "end": v(-5424.27, 267.64) * mm});
            skArc(sketch, "E35.68.0.2", {"start": v(-5424.27, 267.64) * mm, "mid": v(-5431.28, 276.19) * mm, "end": v(-5441.87, 279.4) * mm});
            skLineSegment(sketch, "E35.68.0.3", {"start": v(-5441.87, 279.4) * mm, "end": v(-5454.73, 279.4) * mm});
            skArc(sketch, "E35.68.0.4", {"start": v(-5454.73, 279.4) * mm, "mid": v(-5465.32, 276.19) * mm, "end": v(-5472.33, 267.64) * mm});
            skLineSegment(sketch, "E35.68.0.5", {"start": v(-5472.33, 267.64) * mm, "end": v(-5477.6, 254.92) * mm});
            skArc(sketch, "E35.69.0.0", {"start": v(-5495.2, 254.92) * mm, "mid": v(-5486.4, 249.05) * mm, "end": v(-5477.6, 254.92) * mm});
            skLineSegment(sketch, "E35.69.0.1", {"start": v(-5495.2, 254.92) * mm, "end": v(-5500.47, 267.64) * mm});
            skArc(sketch, "E35.69.0.2", {"start": v(-5500.47, 267.64) * mm, "mid": v(-5507.48, 276.19) * mm, "end": v(-5518.07, 279.4) * mm});
            skLineSegment(sketch, "E35.69.0.3", {"start": v(-5518.07, 279.4) * mm, "end": v(-5530.93, 279.4) * mm});
            skArc(sketch, "E35.69.0.4", {"start": v(-5530.93, 279.4) * mm, "mid": v(-5541.52, 276.19) * mm, "end": v(-5548.53, 267.64) * mm});
            skLineSegment(sketch, "E35.69.0.5", {"start": v(-5548.53, 267.64) * mm, "end": v(-5553.8, 254.92) * mm});
            skArc(sketch, "E35.70.0.0", {"start": v(-5571.4, 254.92) * mm, "mid": v(-5562.6, 249.05) * mm, "end": v(-5553.8, 254.92) * mm});
            skLineSegment(sketch, "E35.70.0.1", {"start": v(-5571.4, 254.92) * mm, "end": v(-5576.67, 267.64) * mm});
            skArc(sketch, "E35.70.0.2", {"start": v(-5576.67, 267.64) * mm, "mid": v(-5583.68, 276.19) * mm, "end": v(-5594.27, 279.4) * mm});
            skLineSegment(sketch, "E35.70.0.3", {"start": v(-5594.27, 279.4) * mm, "end": v(-5607.13, 279.4) * mm});
            skArc(sketch, "E35.70.0.4", {"start": v(-5607.13, 279.4) * mm, "mid": v(-5617.72, 276.19) * mm, "end": v(-5624.73, 267.64) * mm});
            skLineSegment(sketch, "E35.70.0.5", {"start": v(-5624.73, 267.64) * mm, "end": v(-5630, 254.92) * mm});
            skArc(sketch, "E35.71.0.0", {"start": v(-5647.6, 254.92) * mm, "mid": v(-5638.8, 249.05) * mm, "end": v(-5630, 254.92) * mm});
            skLineSegment(sketch, "E35.71.0.1", {"start": v(-5647.6, 254.92) * mm, "end": v(-5652.87, 267.64) * mm});
            skArc(sketch, "E35.71.0.2", {"start": v(-5652.87, 267.64) * mm, "mid": v(-5659.88, 276.19) * mm, "end": v(-5670.47, 279.4) * mm});
            skLineSegment(sketch, "E35.71.0.3", {"start": v(-5670.47, 279.4) * mm, "end": v(-5683.33, 279.4) * mm});
            skArc(sketch, "E35.71.0.4", {"start": v(-5683.33, 279.4) * mm, "mid": v(-5693.92, 276.19) * mm, "end": v(-5700.93, 267.64) * mm});
            skLineSegment(sketch, "E35.71.0.5", {"start": v(-5700.93, 267.64) * mm, "end": v(-5706.2, 254.92) * mm});
            skArc(sketch, "E35.72.0.0", {"start": v(-5723.8, 254.92) * mm, "mid": v(-5715, 249.05) * mm, "end": v(-5706.2, 254.92) * mm});
            skLineSegment(sketch, "E35.72.0.1", {"start": v(-5723.8, 254.92) * mm, "end": v(-5729.07, 267.64) * mm});
            skArc(sketch, "E35.72.0.2", {"start": v(-5729.07, 267.64) * mm, "mid": v(-5736.08, 276.19) * mm, "end": v(-5746.67, 279.4) * mm});
            skLineSegment(sketch, "E35.72.0.3", {"start": v(-5746.67, 279.4) * mm, "end": v(-5759.53, 279.4) * mm});
            skArc(sketch, "E35.72.0.4", {"start": v(-5759.53, 279.4) * mm, "mid": v(-5770.12, 276.19) * mm, "end": v(-5777.13, 267.64) * mm});
            skLineSegment(sketch, "E35.72.0.5", {"start": v(-5777.13, 267.64) * mm, "end": v(-5782.4, 254.92) * mm});
            skArc(sketch, "E35.73.0.0", {"start": v(-5800, 254.92) * mm, "mid": v(-5791.2, 249.05) * mm, "end": v(-5782.4, 254.92) * mm});
            skLineSegment(sketch, "E35.73.0.1", {"start": v(-5800, 254.92) * mm, "end": v(-5805.27, 267.64) * mm});
            skArc(sketch, "E35.73.0.2", {"start": v(-5805.27, 267.64) * mm, "mid": v(-5812.28, 276.19) * mm, "end": v(-5822.87, 279.4) * mm});
            skLineSegment(sketch, "E35.73.0.3", {"start": v(-5822.87, 279.4) * mm, "end": v(-5835.73, 279.4) * mm});
            skArc(sketch, "E35.73.0.4", {"start": v(-5835.73, 279.4) * mm, "mid": v(-5846.32, 276.19) * mm, "end": v(-5853.33, 267.64) * mm});
            skLineSegment(sketch, "E35.73.0.5", {"start": v(-5853.33, 267.64) * mm, "end": v(-5858.6, 254.92) * mm});
            skArc(sketch, "E35.74.0.0", {"start": v(-5876.2, 254.92) * mm, "mid": v(-5867.4, 249.05) * mm, "end": v(-5858.6, 254.92) * mm});
            skLineSegment(sketch, "E35.74.0.1", {"start": v(-5876.2, 254.92) * mm, "end": v(-5881.47, 267.64) * mm});
            skArc(sketch, "E35.74.0.2", {"start": v(-5881.47, 267.64) * mm, "mid": v(-5888.48, 276.19) * mm, "end": v(-5899.07, 279.4) * mm});
            skLineSegment(sketch, "E35.74.0.3", {"start": v(-5899.07, 279.4) * mm, "end": v(-5911.93, 279.4) * mm});
            skArc(sketch, "E35.74.0.4", {"start": v(-5911.93, 279.4) * mm, "mid": v(-5922.52, 276.19) * mm, "end": v(-5929.53, 267.64) * mm});
            skLineSegment(sketch, "E35.74.0.5", {"start": v(-5929.53, 267.64) * mm, "end": v(-5934.8, 254.92) * mm});
            skArc(sketch, "E35.75.0.0", {"start": v(-5952.4, 254.92) * mm, "mid": v(-5943.6, 249.05) * mm, "end": v(-5934.8, 254.92) * mm});
            skLineSegment(sketch, "E35.75.0.1", {"start": v(-5952.4, 254.92) * mm, "end": v(-5957.67, 267.64) * mm});
            skArc(sketch, "E35.75.0.2", {"start": v(-5957.67, 267.64) * mm, "mid": v(-5964.68, 276.19) * mm, "end": v(-5975.27, 279.4) * mm});
            skLineSegment(sketch, "E35.75.0.3", {"start": v(-5975.27, 279.4) * mm, "end": v(-5988.13, 279.4) * mm});
            skArc(sketch, "E35.75.0.4", {"start": v(-5988.13, 279.4) * mm, "mid": v(-5998.72, 276.19) * mm, "end": v(-6005.73, 267.64) * mm});
            skLineSegment(sketch, "E35.75.0.5", {"start": v(-6005.73, 267.64) * mm, "end": v(-6011, 254.92) * mm});
            skArc(sketch, "E35.76.0.0", {"start": v(-6028.6, 254.92) * mm, "mid": v(-6019.8, 249.05) * mm, "end": v(-6011, 254.92) * mm});
            skLineSegment(sketch, "E35.76.0.1", {"start": v(-6028.6, 254.92) * mm, "end": v(-6033.87, 267.64) * mm});
            skArc(sketch, "E35.76.0.2", {"start": v(-6033.87, 267.64) * mm, "mid": v(-6040.88, 276.19) * mm, "end": v(-6051.47, 279.4) * mm});
            skLineSegment(sketch, "E35.76.0.3", {"start": v(-6051.47, 279.4) * mm, "end": v(-6064.33, 279.4) * mm});
            skArc(sketch, "E35.76.0.4", {"start": v(-6064.33, 279.4) * mm, "mid": v(-6072.85, 277.39) * mm, "end": v(-6079.57, 271.78) * mm});
            skLineSegment(sketch, "E35.direction1", {"start": v(-237.4, 254.92) * mm, "end": v(-313.6, 254.92) * mm, "construction": true});
            skLineSegment(sketch, "E36", {"start": v(-6096, 228.6) * mm, "end": v(-6111.78, 266.7) * mm});
            skLineSegment(sketch, "E37", {"start": v(-6111.78, 266.7) * mm, "end": v(-6248.4, 266.7) * mm});
            skLineSegment(sketch, "E38", {"start": v(-6248.4, 266.7) * mm, "end": v(-6248.4, 271.78) * mm});
            skLineSegment(sketch, "E39", {"start": v(-6248.4, 271.78) * mm, "end": v(-6079.57, 271.78) * mm});
            skPoint(sketch, "E40.orphan", {"position": v(-6081.93, 267.64) * mm});
            skLineSegment(sketch, "E41", {"start": v(0, 233.68) * mm, "end": v(0, 228.6) * mm});
            skSolve(sketch);
        }
        {
            var Q0;
            Q0=makeQuery(id+"F6.imprint","IMPRINT",FACE,{"disambiguationData":[TD([[makeQuery(id+"F6.imprint","IMPRINT",EDGE,{"derivedFrom":sQuery(id+"F6.wireOp",EDGE,"E11")}),-1.0]])]});
            var Q1;
            Q1=sQuery(id+"F6.wireOp",EDGE,"E10");
            revolve(context, id + "F7", {"entities" : qUnion([Q0]), "axis" : qUnion([Q1]), "revolveType" : RevolveType.FULL});
        }
        {
            var Q0;
            Q0=qCreatedBy(makeId("Front.planeOp"),FACE);
            cPlane(context, id + "F8", {"entities" : qUnion([Q0]), "cplaneType" : CPlaneType.OFFSET, "offset" : 2540 * mm, "oppositeDirection" : true, "width" : 152.4 * mm, "height" : 152.4 * mm});
        }
        {
            var Q0;
            Q0=qCreatedBy(id+"F8.planeOp",FACE);
            var sketch = newSketch(context, id + "F9", { "sketchPlane" : qUnion([Q0])});
            skCircle(sketch, "E42", {"center": v(0, 0) * mm, "radius": 111.76 * mm});
            skCircle(sketch, "E43", {"center": v(0, 0) * mm, "radius": 106.68 * mm});
            skSolve(sketch);
        }
        {
            var Q0;
            Q0=qCreatedBy(makeId("Right.planeOp"),FACE);
            var sketch = newSketch(context, id + "F10", { "sketchPlane" : qUnion([Q0])});
            skLineSegment(sketch, "E44", {"start": v(2540, 0) * mm, "end": v(2641.6, 0) * mm});
            skLineSegment(sketch, "E45", {"start": v(2755.9, -114.3) * mm, "end": v(2755.9, -215.9) * mm});
            skPoint(sketch, "E46.visualSharp", {"position": v(2755.9, 0) * mm});
            skArc(sketch, "E46.filletArc", {"start": v(2755.9, -114.3) * mm, "mid": v(2722.42, -33.48) * mm, "end": v(2641.6, 0) * mm});
            skSolve(sketch);
        }
        {
            var Q0;
            Q0=makeQuery(id+"F9.imprint","IMPRINT",FACE,{"disambiguationData":[TD([[makeQuery(id+"F9.imprint","IMPRINT",EDGE,{"derivedFrom":sQuery(id+"F9.wireOp",EDGE,"E42")}),1.0]])]});
            var Q1;
            Q1=sQuery(id+"F10.wireOp",EDGE,"E44");
            var Q2;
            Q2=sQuery(id+"F10.wireOp",EDGE,"E45");
            var Q3;
            Q3=sQuery(id+"F10.wireOp",EDGE,"E46.filletArc");
            sweep(context, id + "F11", {"profiles" : qUnion([Q0]), "path" : qUnion([Q1, Q2, Q3])});
        }
    });
